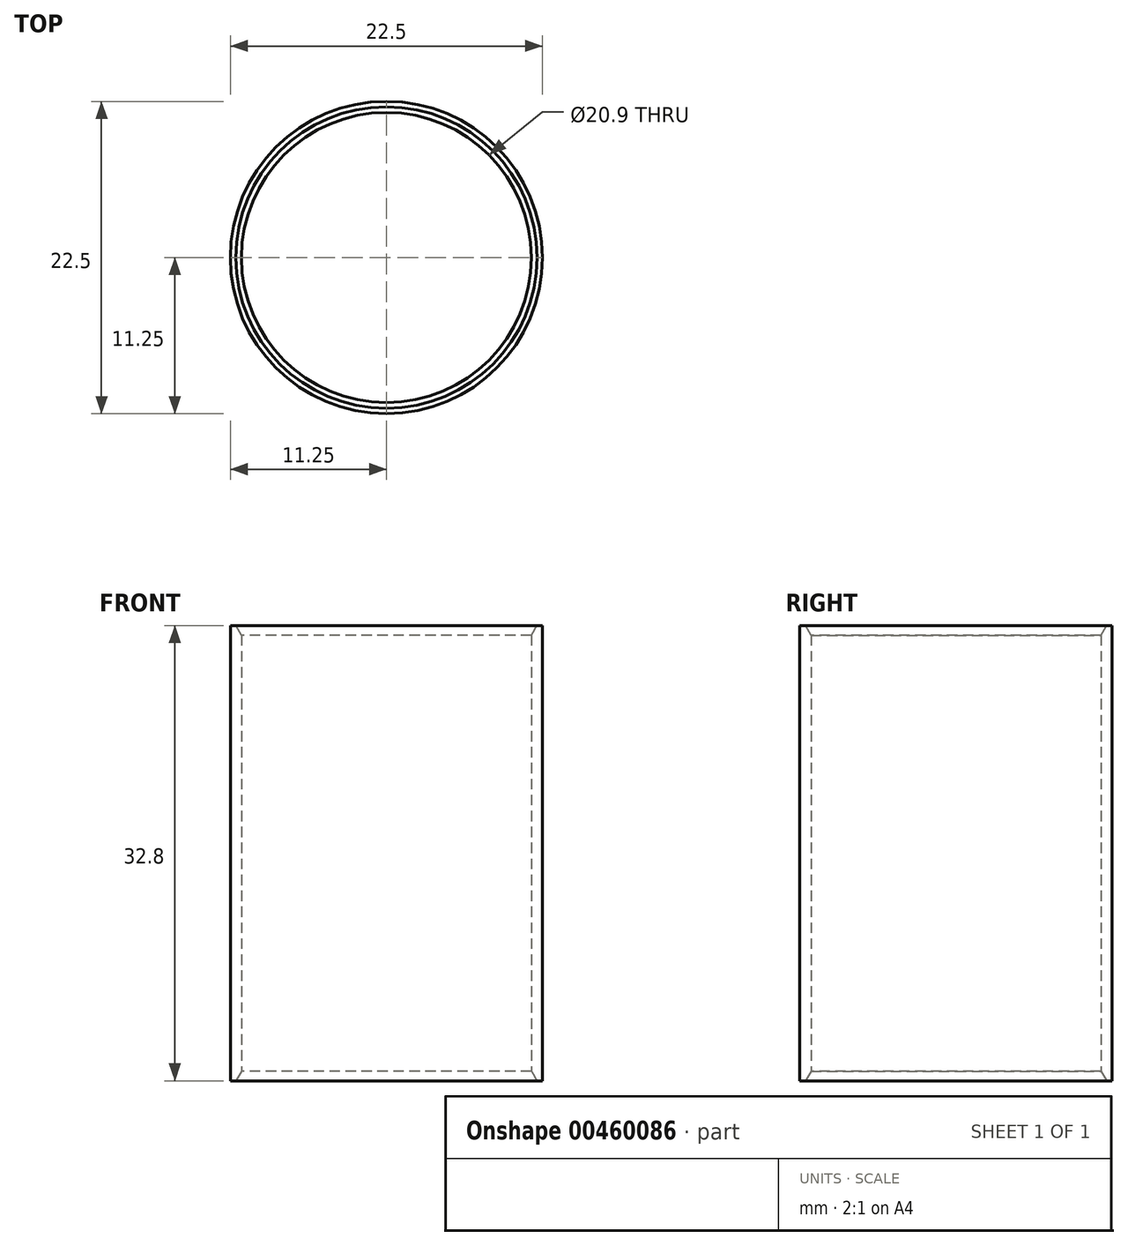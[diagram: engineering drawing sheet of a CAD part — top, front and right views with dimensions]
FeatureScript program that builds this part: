
annotation { "Feature Type Name" : "Feature", "Feature Type Description" : "" }
export const myFeature = defineFeature(function(context is Context, id is Id, definition is map)
    precondition{}
    {
        {
            var Q0;
            Q0=qCreatedBy(makeId("Top.planeOp"),FACE);
            var sketch = newSketch(context, id + "F0", { "sketchPlane" : qUnion([Q0])});
            skCircle(sketch, "E0", {"center": v(0, 0) * mm, "radius": 11.25 * mm});
            skCircle(sketch, "E1.0", {"center": v(0, 0) * mm, "radius": 10.45 * mm});
            skSolve(sketch);
        }
        {
            var Q0;
            Q0=makeQuery(id+"F0.imprint","IMPRINT",FACE,{"disambiguationData":[TD([[makeQuery(id+"F0.imprint","IMPRINT",EDGE,{"derivedFrom":sQuery(id+"F0.wireOp",EDGE,"E0")}),1.0]])]});
            extrude(context, id + "F1", {"entities" : qUnion([Q0]), "depth" : 32.8 * mm});
        }
        {
            var Q0;
            Q0=makeQuery(id+"F1.opExtrude","CAP_EDGE",EDGE,{"disambiguationData":[OSD([sQuery(id+"F0.wireOp",EDGE,"E1.0")])],"isStart":false});
            var Q1;
            Q1=makeQuery(id+"F1.opExtrude","CAP_EDGE",EDGE,{"disambiguationData":[OSD([sQuery(id+"F0.wireOp",EDGE,"E1.0")])],"isStart":true});
            chamfer(context, id + "F2", {"entities" : qUnion([Q0, Q1]), "chamferType" : ChamferType.OFFSET_ANGLE, "width" : 0.7 * mm, "oppositeDirection" : false, "angle" : 30 * degree, "tangentPropagation" : true});
        }
    });
